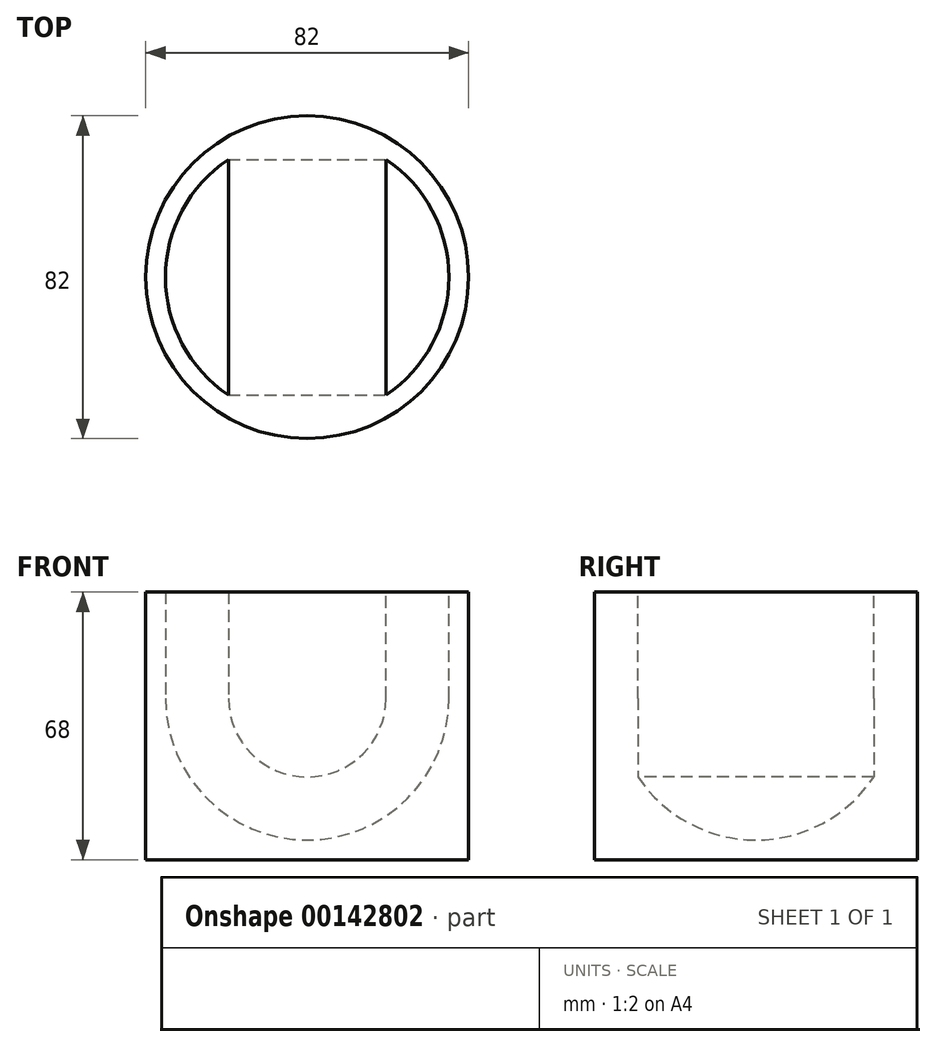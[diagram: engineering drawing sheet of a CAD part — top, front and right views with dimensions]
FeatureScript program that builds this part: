
annotation { "Feature Type Name" : "Feature", "Feature Type Description" : "" }
export const myFeature = defineFeature(function(context is Context, id is Id, definition is map)
    precondition{}
    {
        {
            var Q0;
            Q0=qCreatedBy(makeId("Top.planeOp"),FACE);
            var sketch = newSketch(context, id + "F0", { "sketchPlane" : qUnion([Q0])});
            skCircle(sketch, "E0", {"center": v(0, 0) * mm, "radius": 41 * mm});
            skSolve(sketch);
        }
        {
            var Q0;
            Q0 = qSketchRegion(id + "F0", true);
            extrude(context, id + "F1", {"entities" : qUnion([Q0]), "depth" : 68 * mm});
        }
        {
            var Q0;
            Q0=qCreatedBy(makeId("Front.planeOp"),FACE);
            var sketch = newSketch(context, id + "F2", { "sketchPlane" : qUnion([Q0])});
            skLineSegment(sketch, "E1", {"start": v(-36, 68) * mm, "end": v(-36, 41) * mm});
            skArc(sketch, "E2", {"start": v(-36, 41) * mm, "mid": v(0, 5) * mm, "end": v(36, 41) * mm});
            skPoint(sketch, "E3", {"position": v(0, 5) * mm});
            skLineSegment(sketch, "E4", {"start": v(36, 41) * mm, "end": v(36, 93.78) * mm});
            skSolve(sketch);
        }
        {
            var Q0;
            Q0=makeQuery(id+"F1.opExtrude","CAP_FACE",FACE,{"disambiguationData":[OSD([sQuery(id+"F0.wireOp",EDGE,"E0")])],"isStart":false});
            cPlane(context, id + "F3", {"entities" : qUnion([Q0]), "cplaneType" : CPlaneType.OFFSET, "offset" : 15 * mm, "width" : 150 * mm, "height" : 150 * mm});
        }
        {
            var Q0;
            Q0=qCreatedBy(id+"F3.planeOp",FACE);
            var sketch = newSketch(context, id + "F4", { "sketchPlane" : qUnion([Q0])});
            skArc(sketch, "E5", {"start": v(20, -29.93) * mm, "mid": v(36, 0) * mm, "end": v(20, 29.93) * mm});
            skPoint(sketch, "E6", {"position": v(36, 0) * mm});
            skLineSegment(sketch, "E7", {"start": v(20, 29.93) * mm, "end": v(20, -29.93) * mm});
            skSolve(sketch);
        }
        {
            var Q0;
            Q0 = qSketchRegion(id + "F4", true);
            extrude(context, id + "F5", {"entities" : qUnion([Q0]), "operationType" : NewBodyOperationType.REMOVE, "endBound" : BoundingType.UP_TO_NEXT, "oppositeDirection" : true, "depth" : 25 * mm});
        }
        {
            var Q0;
            Q0 = qSketchRegion(id + "F4", true);
            var Q1;
            Q1 = qConstructionFilter(qBodyType(qCreatedBy(id + "F2" ,EDGE), BodyType.WIRE), ConstructionObject.NO);
            sweep(context, id + "F6", {"operationType" : NewBodyOperationType.REMOVE, "profiles" : qUnion([Q0]), "path" : qUnion([Q1])});
        }
    });
